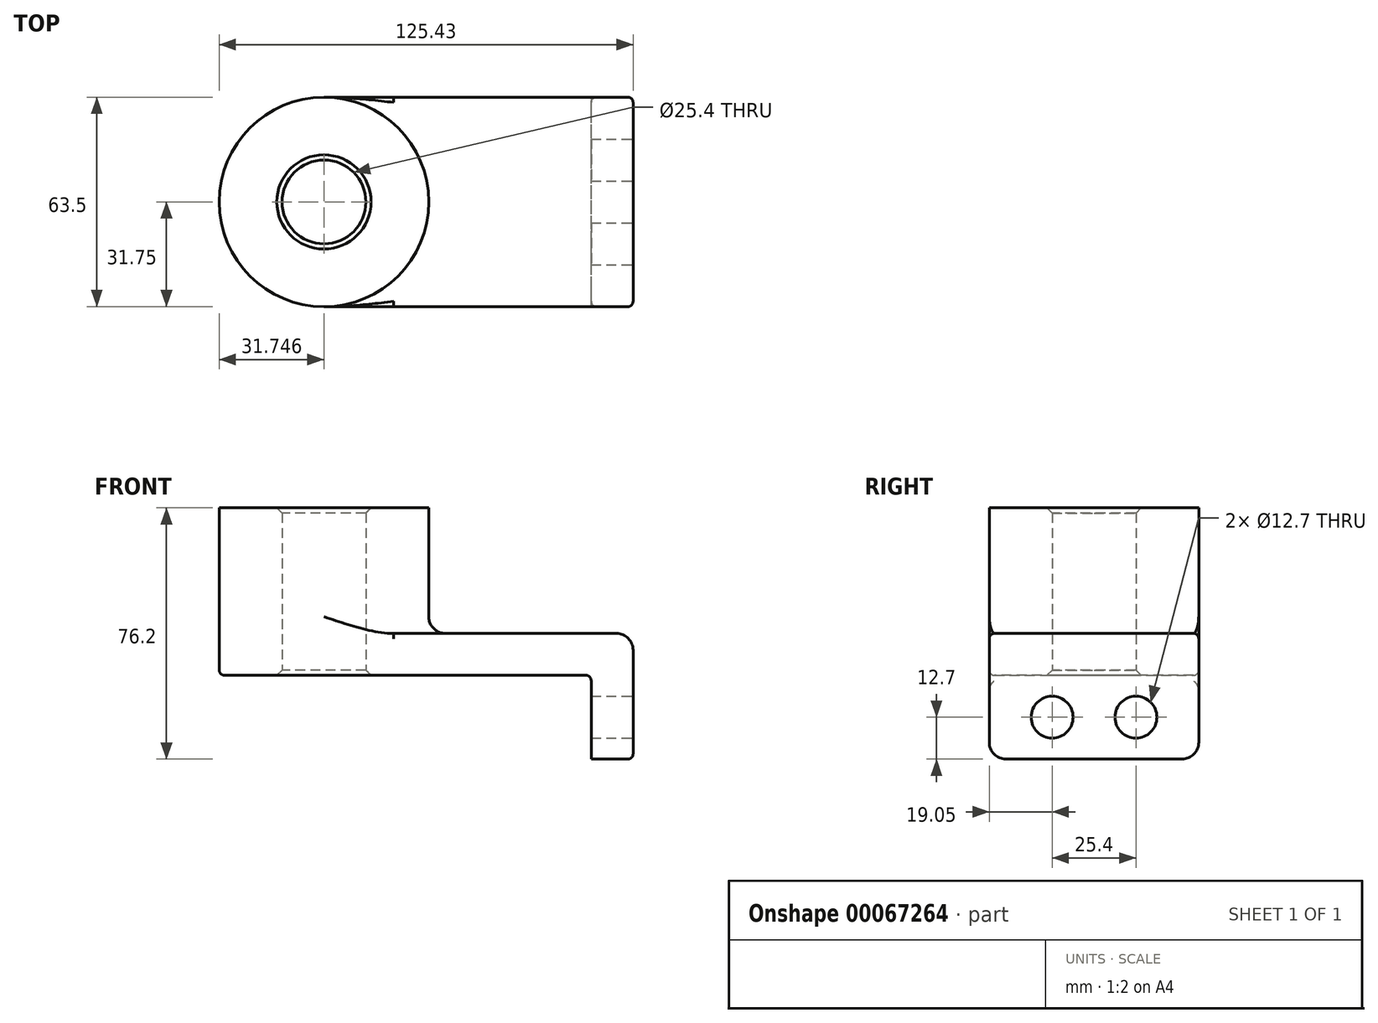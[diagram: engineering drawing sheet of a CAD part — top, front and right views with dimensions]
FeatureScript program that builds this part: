
annotation { "Feature Type Name" : "Feature", "Feature Type Description" : "" }
export const myFeature = defineFeature(function(context is Context, id is Id, definition is map)
    precondition{}
    {
        {
            var Q0;
            Q0=qCreatedBy(makeId("Top.planeOp"),FACE);
            var sketch = newSketch(context, id + "F0", { "sketchPlane" : qUnion([Q0])});
            skLineSegment(sketch, "E0.rect.bottom", {"start": v(-46.84, 31.75) * mm, "end": v(46.84, 31.75) * mm});
            skLineSegment(sketch, "E0.rect.top", {"start": v(-46.84, -31.75) * mm, "end": v(46.84, -31.75) * mm});
            skLineSegment(sketch, "E0.rect.left", {"start": v(-46.84, 31.75) * mm, "end": v(-46.84, -31.75) * mm});
            skLineSegment(sketch, "E0.rect.right", {"start": v(46.84, 31.75) * mm, "end": v(46.84, -31.75) * mm});
            skPoint(sketch, "E0.rect.middle", {"position": v(0, 0) * mm});
            skCircle(sketch, "E1", {"center": v(-46.84, 0) * mm, "radius": 31.75 * mm});
            skCircle(sketch, "E2", {"center": v(-46.84, 0) * mm, "radius": 12.7 * mm});
            skSolve(sketch);
        }
        {
            var Q0;
            Q0 = qSketchRegion(id + "F0", true);
            extrude(context, id + "F1", {"entities" : qUnion([Q0]), "depth" : 12.7 * mm});
        }
        {
            var Q0;
            {var subQ1=sQuery(id+"F0.wireOp",EDGE,"E0.rect.left");var subQ3=sQuery(id+"F0.wireOp",EDGE,"E2");var subQ4=makeQuery(id+"F0.imprint","INTERSECT",VERTEX,{"disambiguationData":[OD(0.0)],"derivedFrom":[subQ1,subQ3]});Q0=makeQuery(id+"F0.imprint","IMPRINT",FACE,{"disambiguationData":[TD([[makeQuery(id+"F0.imprint","IMPRINT",EDGE,{"disambiguationData":[TD([[subQ4,1.0]])],"derivedFrom":subQ3}),-1.0]])]});}
            var Q1;
            {var subQ1=sQuery(id+"F0.wireOp",EDGE,"E0.rect.left");var subQ3=sQuery(id+"F0.wireOp",EDGE,"E2");var subQ4=makeQuery(id+"F0.imprint","INTERSECT",VERTEX,{"disambiguationData":[OD(0.0)],"derivedFrom":[subQ1,subQ3]});Q1=makeQuery(id+"F0.imprint","IMPRINT",FACE,{"disambiguationData":[TD([[makeQuery(id+"F0.imprint","IMPRINT",EDGE,{"disambiguationData":[TD([[subQ4,-1.0]])],"derivedFrom":subQ3}),-1.0]])]});}
            extrude(context, id + "F2", {"entities" : qUnion([Q0, Q1]), "operationType" : NewBodyOperationType.ADD, "depth" : 50.8 * mm});
        }
        {
            var Q0;
            Q0=makeQuery(id+"F1.opExtrude","SWEPT_FACE",FACE,{"disambiguationData":[OSD([sQuery(id+"F0.wireOp",EDGE,"E0.rect.right")])]});
            var sketch = newSketch(context, id + "F3", { "sketchPlane" : qUnion([Q0])});
            skLineSegment(sketch, "E3.bottom", {"start": v(-31.75, 12.7) * mm, "end": v(31.75, 12.7) * mm});
            skLineSegment(sketch, "E3.top", {"start": v(-31.75, -25.4) * mm, "end": v(31.75, -25.4) * mm});
            skLineSegment(sketch, "E3.left", {"start": v(-31.75, 12.7) * mm, "end": v(-31.75, -25.4) * mm});
            skLineSegment(sketch, "E3.right", {"start": v(31.75, 12.7) * mm, "end": v(31.75, -25.4) * mm});
            skCircle(sketch, "E4", {"center": v(-12.7, -12.7) * mm, "radius": 6.35 * mm});
            skLineSegment(sketch, "E5", {"start": v(0, 0) * mm, "end": v(0, -25.4) * mm, "construction": true});
            skCircle(sketch, "E6.MirrorC", {"center": v(12.7, -12.7) * mm, "radius": 6.35 * mm});
            skSolve(sketch);
        }
        {
            var Q0;
            Q0 = qSketchRegion(id + "F3", true);
            extrude(context, id + "F4", {"entities" : qUnion([Q0]), "operationType" : NewBodyOperationType.ADD, "oppositeDirection" : true, "depth" : 12.7 * mm});
        }
        {
            var Q0;
            {var subQ0=sQuery(id+"F0.wireOp",EDGE,"E1");Q0=makeQuery(id+"F2.boolean.opBoolean","INTERSECT",EDGE,{"derivedFrom":[makeQuery(id+"F1.opExtrude","CAP_FACE",FACE,{"disambiguationData":[OSD([sQuery(id+"F0.wireOp",EDGE,"E0.rect.bottom"),sQuery(id+"F0.wireOp",EDGE,"E0.rect.top"),sQuery(id+"F0.wireOp",EDGE,"E0.rect.right"),subQ0,sQuery(id+"F0.wireOp",EDGE,"E2")])],"isStart":false}),makeQuery(id+"F2.opExtrude","SWEPT_FACE",FACE,{"disambiguationData":[OSD([subQ0])]})]});}
            var Q1;
            Q1=makeQuery(id+"F1.opExtrude","CAP_EDGE",EDGE,{"disambiguationData":[OSD([sQuery(id+"F0.wireOp",EDGE,"E0.rect.right")])],"isStart":false});
            var Q2;
            Q2=makeQuery(id+"F4.opExtrude","SWEPT_EDGE",EDGE,{"disambiguationData":[OSD([sQuery(id+"F3.wireOp",EDGE,"E3.top"),sQuery(id+"F3.wireOp",EDGE,"E3.left")])]});
            var Q3;
            Q3=makeQuery(id+"F4.opExtrude","SWEPT_EDGE",EDGE,{"disambiguationData":[OSD([sQuery(id+"F3.wireOp",EDGE,"E3.top"),sQuery(id+"F3.wireOp",EDGE,"E3.right")])]});
            fillet(context, id + "F5", {"entities" : qUnion([Q0, Q1, Q2, Q3]), "radius" : 5.08 * mm, "tangentPropagation" : true, "allowEdgeOverflow" : false});
        }
        {
            var Q0;
            Q0=makeQuery(id+"F1.opExtrude","CAP_EDGE",EDGE,{"disambiguationData":[OSD([sQuery(id+"F0.wireOp",EDGE,"E0.rect.top")])],"isStart":false});
            var Q1;
            Q1=makeQuery(id+"F1.opExtrude","CAP_EDGE",EDGE,{"disambiguationData":[OSD([sQuery(id+"F0.wireOp",EDGE,"E0.rect.top")])],"isStart":true});
            var Q2;
            Q2=makeQuery(id+"F4.boolean.opBoolean","INTERSECT",EDGE,{"derivedFrom":[makeQuery(id+"F1.opExtrude","CAP_FACE",FACE,{"disambiguationData":[OSD([sQuery(id+"F0.wireOp",EDGE,"E0.rect.bottom"),sQuery(id+"F0.wireOp",EDGE,"E0.rect.top"),sQuery(id+"F0.wireOp",EDGE,"E0.rect.right"),sQuery(id+"F0.wireOp",EDGE,"E1"),sQuery(id+"F0.wireOp",EDGE,"E2")])],"isStart":true}),makeQuery(id+"F4.opExtrude","CAP_FACE",FACE,{"disambiguationData":[OSD([sQuery(id+"F3.wireOp",EDGE,"E3.bottom"),sQuery(id+"F3.wireOp",EDGE,"E3.top"),sQuery(id+"F3.wireOp",EDGE,"E3.left"),sQuery(id+"F3.wireOp",EDGE,"E3.right"),sQuery(id+"F3.wireOp",EDGE,"E4"),sQuery(id+"F3.wireOp",EDGE,"E6.MirrorC")])],"isStart":false})]});
            fillet(context, id + "F6", {"entities" : qUnion([Q0, Q1, Q2]), "radius" : 1.59 * mm, "tangentPropagation" : true, "allowEdgeOverflow" : false});
        }
        {
            var Q0;
            {var subQ0=sQuery(id+"F0.wireOp",EDGE,"E2");Q0=makeQuery(id+"F2.boolean.opBoolean","MERGE",FACE,{"derivedFrom":[makeQuery(id+"F1.opExtrude","SWEPT_FACE",FACE,{"disambiguationData":[OSD([subQ0])]}),makeQuery(id+"F2.opExtrude","SWEPT_FACE",FACE,{"disambiguationData":[OSD([subQ0])]})]});}
            chamfer(context, id + "F7", {"entities" : qUnion([Q0]), "width" : 1.59 * mm, "tangentPropagation" : true});
        }
    });
